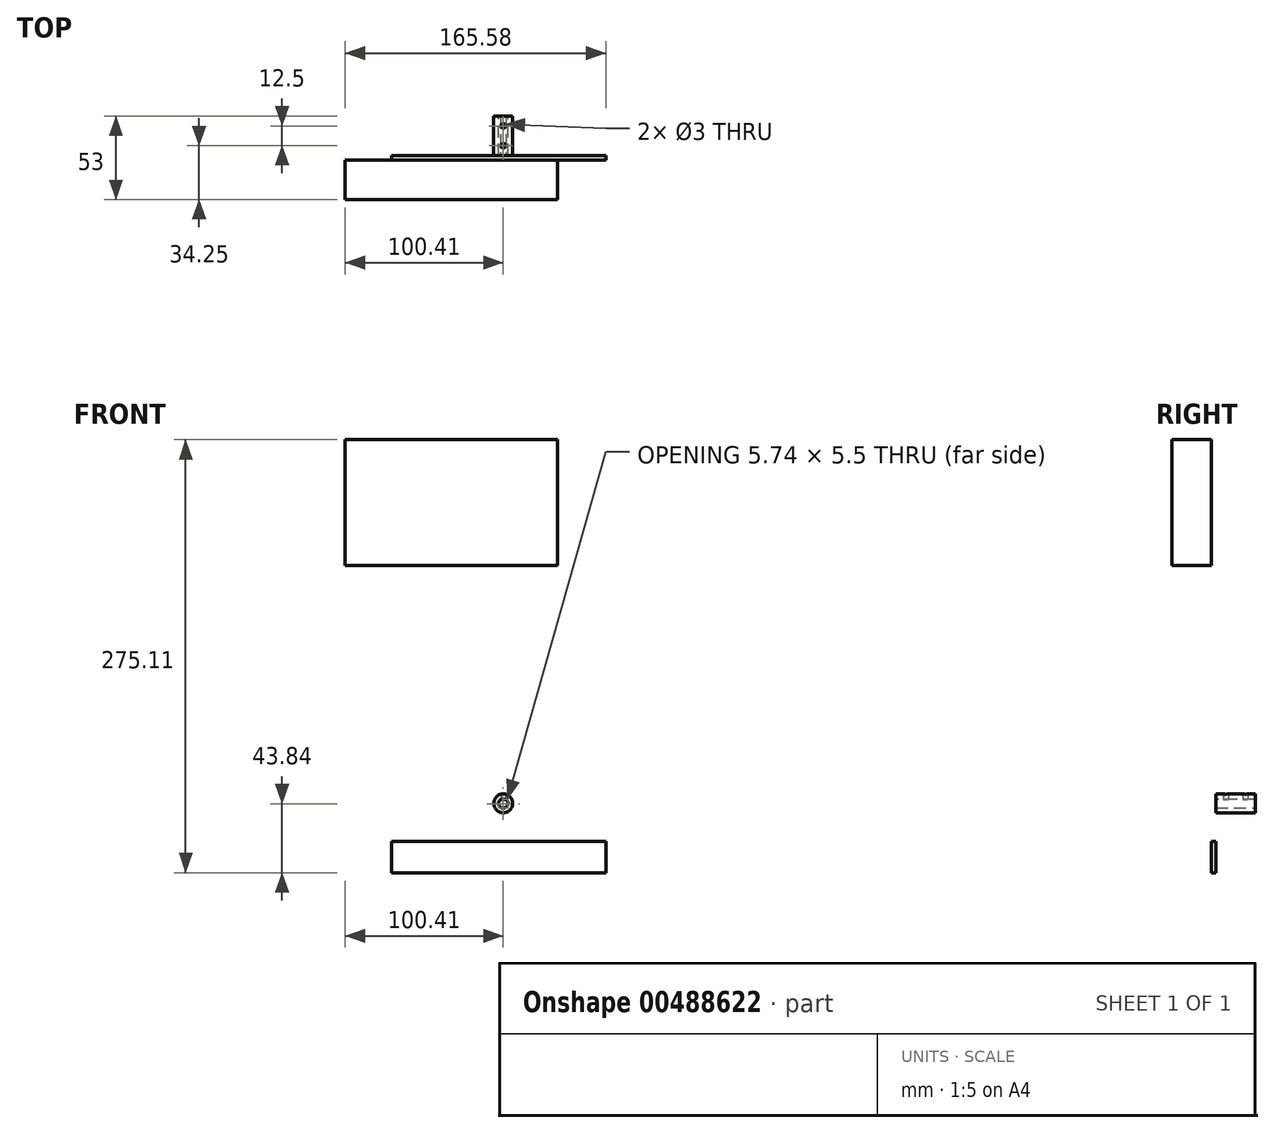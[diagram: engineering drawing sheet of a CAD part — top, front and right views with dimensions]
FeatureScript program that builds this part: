
annotation { "Feature Type Name" : "Feature", "Feature Type Description" : "" }
export const myFeature = defineFeature(function(context is Context, id is Id, definition is map)
    precondition{}
    {
        {
            var Q0;
            Q0=qCreatedBy(makeId("Front.planeOp"),FACE);
            var sketch = newSketch(context, id + "F0", { "sketchPlane" : qUnion([Q0])});
            skCircle(sketch, "E0", {"center": v(0, 0) * mm, "radius": 6 * mm});
            skSolve(sketch);
        }
        {
            var Q0;
            Q0=makeQuery(id+"F0.imprint","IMPRINT",FACE,{"disambiguationData":[TD([[makeQuery(id+"F0.imprint","IMPRINT",EDGE,{"derivedFrom":sQuery(id+"F0.wireOp",EDGE,"E0")}),1.0]])]});
            extrude(context, id + "F1", {"entities" : qUnion([Q0]), "depth" : 25 * mm});
        }
        {
            var Q0;
            Q0=qCreatedBy(makeId("Front.planeOp"),FACE);
            var sketch = newSketch(context, id + "F2", { "sketchPlane" : qUnion([Q0])});
            skCircle(sketch, "E1", {"center": v(0, 0) * mm, "radius": 3 * mm});
            skSolve(sketch);
        }
        {
            var Q0;
            Q0=makeQuery(id+"F2.imprint","IMPRINT",FACE,{"disambiguationData":[TD([[makeQuery(id+"F2.imprint","IMPRINT",EDGE,{"derivedFrom":sQuery(id+"F2.wireOp",EDGE,"E1")}),1.0]])]});
            var Q1;
            Q1=sQuery(id+"F2.wireOp",EDGE,"E1");
            var Q2;
            Q2=makeQuery(id+"F1.opExtrude","CAP_FACE",FACE,{"disambiguationData":[OSD([sQuery(id+"F0.wireOp",EDGE,"E0")])],"isStart":false});
            extrude(context, id + "F3", {"entities" : qUnion([Q0]), "operationType" : NewBodyOperationType.REMOVE, "surfaceEntities" : qUnion([Q1]), "endBound" : BoundingType.UP_TO_SURFACE, "endBoundEntityFace" : qUnion([Q2]), "depth" : 25 * mm});
        }
        {
            var Q0;
            Q0=makeQuery(id+"F1.opExtrude","CAP_FACE",FACE,{"disambiguationData":[OSD([sQuery(id+"F0.wireOp",EDGE,"E0")])],"isStart":false});
            var sketch = newSketch(context, id + "F4", { "sketchPlane" : qUnion([Q0])});
            skLineSegment(sketch, "E2", {"start": v(0, 2.5) * mm, "end": v(-1.66, 2.5) * mm});
            skLineSegment(sketch, "E3", {"start": v(-1.66, 2.5) * mm, "end": v(1.66, 2.5) * mm});
            skSolve(sketch);
        }
        {
            var Q0;
            Q0=qSketchRegion(id+"F4",true);
            var Q1;
            {var subQ0=sQuery(id+"F4.wireOp",EDGE,"E3");var subQ3=makeQuery(id+"F4.imprint","IMPRINT",VERTEX,{"derivedFrom":subQ0});Q1=makeQuery(id+"F4.imprint","IMPRINT",FACE,{"disambiguationData":[TD([[makeQuery(id+"F4.imprint","IMPRINT",EDGE,{"disambiguationData":[TD([[subQ3,1.0]])],"derivedFrom":subQ0}),1.0]])]});}
            var Q2;
            Q2=makeQuery(id+"F1.opExtrude","CAP_FACE",FACE,{"disambiguationData":[OSD([sQuery(id+"F0.wireOp",EDGE,"E0")])],"isStart":true});
            extrude(context, id + "F5", {"entities" : qUnion([Q0, Q1]), "operationType" : NewBodyOperationType.ADD, "endBound" : BoundingType.UP_TO_SURFACE, "oppositeDirection" : true, "endBoundEntityFace" : qUnion([Q2]), "depth" : 25 * mm});
        }
        {
            var Q0;
            Q0=makeQuery(id+"F5.opExtrude","SWEPT_FACE",FACE,{"disambiguationData":[OSD([sQuery(id+"F4.wireOp",EDGE,"E3")])]});
            var sketch = newSketch(context, id + "F6", { "sketchPlane" : qUnion([Q0])});
            skLineSegment(sketch, "E4", {"start": v(-1.66, 12.5) * mm, "end": v(1.66, 12.5) * mm, "construction": true});
            skLineSegment(sketch, "E5", {"start": v(0, 12.5) * mm, "end": v(0, 25) * mm, "construction": true});
            skLineSegment(sketch, "E6", {"start": v(0, 12.5) * mm, "end": v(0, 0) * mm, "construction": true});
            skCircle(sketch, "E7", {"center": v(0, 18.75) * mm, "radius": 1.5 * mm});
            skCircle(sketch, "E8", {"center": v(0, 6.25) * mm, "radius": 1.5 * mm});
            skSolve(sketch);
        }
        {
            var Q0;
            Q0=makeQuery(id+"F6.imprint","IMPRINT",FACE,{"disambiguationData":[TD([[makeQuery(id+"F6.imprint","IMPRINT",EDGE,{"derivedFrom":sQuery(id+"F6.wireOp",EDGE,"E7")}),1.0]])]});
            var Q1;
            Q1=makeQuery(id+"F6.imprint","IMPRINT",FACE,{"disambiguationData":[TD([[makeQuery(id+"F6.imprint","IMPRINT",EDGE,{"derivedFrom":sQuery(id+"F6.wireOp",EDGE,"E8")}),1.0]])]});
            extrude(context, id + "F7", {"entities" : qUnion([Q0, Q1]), "operationType" : NewBodyOperationType.REMOVE, "endBound" : BoundingType.UP_TO_NEXT, "oppositeDirection" : true, "depth" : 25 * mm});
        }
        {
            var Q0;
            {var subQ0=sQuery(id+"F0.wireOp",EDGE,"E0");Q0=makeQuery(id+"F5.boolean.opBoolean","MERGE",FACE,{"derivedFrom":[makeQuery(id+"F1.opExtrude","CAP_FACE",FACE,{"disambiguationData":[OSD([subQ0])],"isStart":false}),makeQuery(id+"F5.opExtrude","CAP_FACE",FACE,{"disambiguationData":[OSD([subQ0,sQuery(id+"F2.wireOp",EDGE,"E1"),sQuery(id+"F4.wireOp",EDGE,"E3")])],"isStart":true})]});}
            var sketch = newSketch(context, id + "F8", { "sketchPlane" : qUnion([Q0])});
            skLineSegment(sketch, "E9.bottom", {"start": v(-70.83, -24.09) * mm, "end": v(65.17, -24.09) * mm});
            skLineSegment(sketch, "E9.top", {"start": v(-70.83, -44.09) * mm, "end": v(65.17, -44.09) * mm});
            skLineSegment(sketch, "E9.left", {"start": v(-70.83, -24.09) * mm, "end": v(-70.83, -44.09) * mm});
            skLineSegment(sketch, "E9.right", {"start": v(65.17, -24.09) * mm, "end": v(65.17, -44.09) * mm});
            skSolve(sketch);
        }
        {
            var Q0;
            Q0=qSketchRegion(id+"F8",true);
            extrude(context, id + "F9", {"entities" : qUnion([Q0]), "depth" : 3 * mm});
        }
        {
            var Q0;
            {var subQ0=sQuery(id+"F0.wireOp",EDGE,"E0");Q0=makeQuery(id+"F5.boolean.opBoolean","MERGE",FACE,{"derivedFrom":[makeQuery(id+"F1.opExtrude","CAP_FACE",FACE,{"disambiguationData":[OSD([subQ0])],"isStart":false}),makeQuery(id+"F5.opExtrude","CAP_FACE",FACE,{"disambiguationData":[OSD([subQ0,sQuery(id+"F2.wireOp",EDGE,"E1"),sQuery(id+"F4.wireOp",EDGE,"E3")])],"isStart":true})]});}
            var sketch = newSketch(context, id + "F10", { "sketchPlane" : qUnion([Q0])});
            skSolve(sketch);
        }
        {
            var Q0;
            Q0=makeQuery(id+"F9.opExtrude","CAP_FACE",FACE,{"disambiguationData":[OSD([sQuery(id+"F8.wireOp",EDGE,"E9.bottom"),sQuery(id+"F8.wireOp",EDGE,"E9.top"),sQuery(id+"F8.wireOp",EDGE,"E9.left"),sQuery(id+"F8.wireOp",EDGE,"E9.right")])],"isStart":false});
            var sketch = newSketch(context, id + "F11", { "sketchPlane" : qUnion([Q0])});
            skLineSegment(sketch, "E10.bottom", {"start": v(-100.41, 231.02) * mm, "end": v(34.59, 231.02) * mm});
            skLineSegment(sketch, "E10.top", {"start": v(-100.41, 151.02) * mm, "end": v(34.59, 151.02) * mm});
            skLineSegment(sketch, "E10.left", {"start": v(-100.41, 231.02) * mm, "end": v(-100.41, 151.02) * mm});
            skLineSegment(sketch, "E10.right", {"start": v(34.59, 231.02) * mm, "end": v(34.59, 151.02) * mm});
            skSolve(sketch);
        }
        {
            var Q0;
            Q0=makeQuery(id+"F11.imprint","IMPRINT",FACE,{"disambiguationData":[TD([[makeQuery(id+"F11.imprint","IMPRINT",EDGE,{"derivedFrom":sQuery(id+"F11.wireOp",EDGE,"E10.bottom")}),-1.0]])]});
            extrude(context, id + "F12", {"entities" : qUnion([Q0]), "depth" : 25 * mm});
        }
    });
